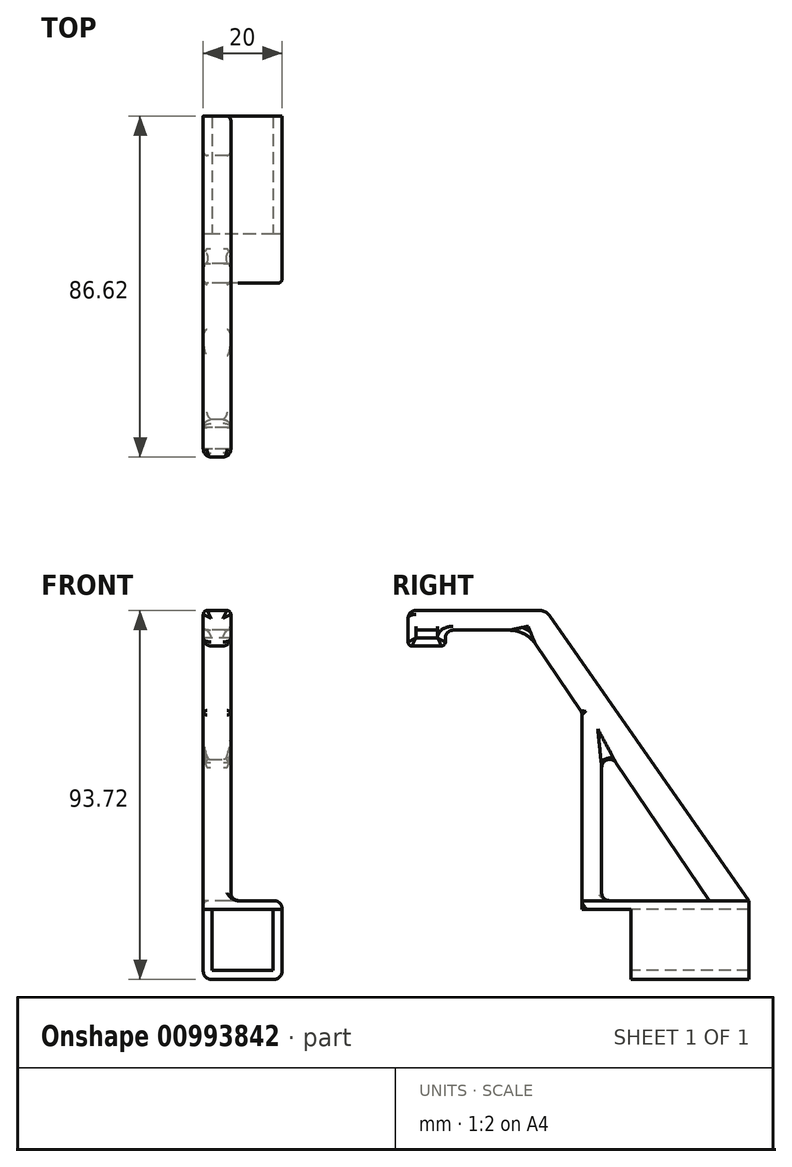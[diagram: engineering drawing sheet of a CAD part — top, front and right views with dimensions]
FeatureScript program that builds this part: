
annotation { "Feature Type Name" : "Feature", "Feature Type Description" : "" }
export const myFeature = defineFeature(function(context is Context, id is Id, definition is map)
    precondition{}
    {
        {
            var Q0;
            Q0=qCreatedBy(makeId("Right.planeOp"),FACE);
            var sketch = newSketch(context, id + "F0", { "sketchPlane" : qUnion([Q0])});
            skLineSegment(sketch, "E0.bottom", {"start": v(-15, 0) * mm, "end": v(15, 0) * mm});
            skLineSegment(sketch, "E0.top", {"start": v(-15, -20) * mm, "end": v(15, -20) * mm});
            skLineSegment(sketch, "E0.left", {"start": v(-15, 0) * mm, "end": v(-15, -20) * mm});
            skLineSegment(sketch, "E0.right", {"start": v(15, 0) * mm, "end": v(15, -20) * mm});
            skLineSegment(sketch, "E1", {"start": v(15, 0) * mm, "end": v(-36.62, 73.72) * mm});
            skLineSegment(sketch, "E2", {"start": v(-36.62, 73.72) * mm, "end": v(-71.62, 73.72) * mm});
            skLineSegment(sketch, "E3", {"start": v(-71.62, 73.72) * mm, "end": v(-71.62, 68.72) * mm});
            skLineSegment(sketch, "E4", {"start": v(-71.62, 68.72) * mm, "end": v(-41.62, 68.72) * mm});
            skLineSegment(sketch, "E5", {"start": v(-41.62, 68.72) * mm, "end": v(5, 0) * mm});
            skLineSegment(sketch, "E6", {"start": v(-15, 0) * mm, "end": v(-27.41, 0) * mm});
            skLineSegment(sketch, "E7", {"start": v(-27.41, 0) * mm, "end": v(-27.41, -2.25) * mm});
            skLineSegment(sketch, "E8", {"start": v(-27.41, -2.25) * mm, "end": v(-15, -2.25) * mm});
            skLineSegment(sketch, "E9", {"start": v(-27.41, 0) * mm, "end": v(-27.41, 47.78) * mm});
            skLineSegment(sketch, "E10", {"start": v(-22.41, 0) * mm, "end": v(-22.41, 40.4) * mm});
            skLineSegment(sketch, "E11", {"start": v(-71.62, 68.72) * mm, "end": v(-71.62, 64.72) * mm});
            skLineSegment(sketch, "E12", {"start": v(-71.62, 64.72) * mm, "end": v(-62.12, 64.72) * mm});
            skLineSegment(sketch, "E13", {"start": v(-62.12, 64.72) * mm, "end": v(-62.12, 68.72) * mm});
            skLineSegment(sketch, "E14", {"start": v(-69.62, 68.72) * mm, "end": v(-69.62, 66.72) * mm});
            skLineSegment(sketch, "E15", {"start": v(-69.62, 66.72) * mm, "end": v(-64.12, 66.72) * mm});
            skLineSegment(sketch, "E16", {"start": v(-64.12, 66.72) * mm, "end": v(-64.12, 68.72) * mm});
            skSolve(sketch);
        }
        {
            var Q0;
            Q0=makeQuery(id+"F0.imprint","IMPRINT",FACE,{"disambiguationData":[TD([[makeQuery(id+"F0.imprint","IMPRINT",EDGE,{"derivedFrom":sQuery(id+"F0.wireOp",EDGE,"E0.top")}),1.0]])]});
            var Q1;
            {var subQ0=sQuery(id+"F0.wireOp",EDGE,"E7");Q1=makeQuery(id+"F0.imprint","IMPRINT",FACE,{"disambiguationData":[TD([[makeQuery(id+"F0.imprint","IMPRINT",EDGE,{"derivedFrom":subQ0}),1.0]])]});}
            extrude(context, id + "F1", {"entities" : qUnion([Q0, Q1]), "depth" : 20 * mm, "offsetDistance" : 25 * mm});
        }
        {
            var Q0;
            {var subQ0=sQuery(id+"F0.wireOp",EDGE,"E1");Q0=makeQuery(id+"F0.imprint","IMPRINT",FACE,{"disambiguationData":[TD([[makeQuery(id+"F0.imprint","IMPRINT",EDGE,{"derivedFrom":subQ0}),1.0]])]});}
            var Q1;
            {var subQ0=sQuery(id+"F0.wireOp",EDGE,"JJyUEpVb-gie7-RlF8-7qWe-H1qUGamomeF3");Q1=makeQuery(id+"F0.imprint","IMPRINT",FACE,{"disambiguationData":[TD([[makeQuery(id+"F0.imprint","IMPRINT",EDGE,{"derivedFrom":subQ0}),-1.0]])]});}
            var Q2;
            {var subQ0=sQuery(id+"F0.wireOp",EDGE,"E9");Q2=makeQuery(id+"F0.imprint","IMPRINT",FACE,{"disambiguationData":[TD([[makeQuery(id+"F0.imprint","IMPRINT",EDGE,{"derivedFrom":subQ0}),-1.0]])]});}
            var Q3;
            {var subQ0=sQuery(id+"F0.wireOp",EDGE,"E11");Q3=makeQuery(id+"F0.imprint","IMPRINT",FACE,{"disambiguationData":[TD([[makeQuery(id+"F0.imprint","IMPRINT",EDGE,{"derivedFrom":subQ0}),1.0]])]});}
            extrude(context, id + "F2", {"entities" : qUnion([Q0, Q1, Q2, Q3]), "operationType" : NewBodyOperationType.ADD, "depth" : 7 * mm, "offsetDistance" : 25 * mm});
        }
        {
            var Q0;
            Q0=makeQuery(id+"F1.opExtrude","SWEPT_FACE",FACE,{"disambiguationData":[OSD([sQuery(id+"F0.wireOp",EDGE,"E0.left")])]});
            var sketch = newSketch(context, id + "F3", { "sketchPlane" : qUnion([Q0])});
            skLineSegment(sketch, "E17.bottom", {"start": v(17.75, -2.25) * mm, "end": v(2.25, -2.25) * mm});
            skLineSegment(sketch, "E17.top", {"start": v(17.75, -17.75) * mm, "end": v(2.25, -17.75) * mm});
            skLineSegment(sketch, "E17.left", {"start": v(17.75, -2.25) * mm, "end": v(17.75, -17.75) * mm});
            skLineSegment(sketch, "E17.right", {"start": v(2.25, -2.25) * mm, "end": v(2.25, -17.75) * mm});
            skPoint(sketch, "E17.middle", {"position": v(0, -10) * mm});
            skSolve(sketch);
        }
        {
            var Q0;
            Q0=makeQuery(id+"F3.imprint","IMPRINT",FACE,{"disambiguationData":[TD([[makeQuery(id+"F3.imprint","IMPRINT",EDGE,{"derivedFrom":sQuery(id+"F3.wireOp",EDGE,"E17.bottom")}),1.0]])]});
            var Q1;
            Q1=makeQuery(id+"F1.opExtrude","SWEPT_FACE",FACE,{"disambiguationData":[OSD([sQuery(id+"F0.wireOp",EDGE,"E0.right")])]});
            extrude(context, id + "F4", {"entities" : qUnion([Q0]), "operationType" : NewBodyOperationType.REMOVE, "endBound" : BoundingType.UP_TO_SURFACE, "oppositeDirection" : true, "depth" : 25 * mm, "endBoundEntityFace" : qUnion([Q1]), "offsetDistance" : 25 * mm});
        }
        {
            var Q0;
            Q0=makeQuery(id+"F2.opExtrude","CAP_EDGE",EDGE,{"disambiguationData":[OSD([sQuery(id+"F0.wireOp",EDGE,"E2")])],"isStart":false});
            var Q1;
            Q1=makeQuery(id+"F2.opExtrude","CAP_EDGE",EDGE,{"disambiguationData":[OSD([sQuery(id+"F0.wireOp",EDGE,"E4")])],"isStart":false});
            var Q2;
            Q2=makeQuery(id+"F2.opExtrude","CAP_EDGE",EDGE,{"disambiguationData":[OSD([sQuery(id+"F0.wireOp",EDGE,"E5")])],"isStart":false});
            var Q3;
            Q3=makeQuery(id+"F2.opExtrude","CAP_EDGE",EDGE,{"disambiguationData":[OSD([sQuery(id+"F0.wireOp",EDGE,"E2")])],"isStart":true});
            var Q4;
            Q4=makeQuery(id+"F2.opExtrude","CAP_EDGE",EDGE,{"disambiguationData":[OSD([sQuery(id+"F0.wireOp",EDGE,"E4")])],"isStart":true});
            var Q5;
            Q5=makeQuery(id+"F2.opExtrude","CAP_EDGE",EDGE,{"disambiguationData":[OSD([sQuery(id+"F0.wireOp",EDGE,"E5")])],"isStart":true});
            var Q6;
            Q6=makeQuery(id+"F2.opExtrude","CAP_EDGE",EDGE,{"disambiguationData":[OSD([sQuery(id+"F0.wireOp",EDGE,"E1")])],"isStart":false});
            var Q7;
            Q7=makeQuery(id+"F2.opExtrude","CAP_EDGE",EDGE,{"disambiguationData":[OSD([sQuery(id+"F0.wireOp",EDGE,"E1")])],"isStart":true});
            var Q8;
            Q8=makeQuery(id+"F2.opExtrude","CAP_EDGE",EDGE,{"disambiguationData":[OSD([sQuery(id+"F0.wireOp",EDGE,"MwvaDB4x-Gc2K-hVEB-6IYb-x19hV3h6sSwj")])],"isStart":false});
            var Q9;
            Q9=makeQuery(id+"F2.opExtrude","CAP_EDGE",EDGE,{"disambiguationData":[OSD([sQuery(id+"F0.wireOp",EDGE,"JJyUEpVb-gie7-RlF8-7qWe-H1qUGamomeF3")])],"isStart":false});
            var Q10;
            Q10=makeQuery(id+"F2.opExtrude","CAP_EDGE",EDGE,{"disambiguationData":[OSD([sQuery(id+"F0.wireOp",EDGE,"MwvaDB4x-Gc2K-hVEB-6IYb-x19hV3h6sSwj")])],"isStart":true});
            var Q11;
            Q11=makeQuery(id+"F2.boolean.opBoolean","MERGE",EDGE,{"derivedFrom":[makeQuery(id+"F1.opExtrude","CAP_EDGE",EDGE,{"disambiguationData":[OSD([sQuery(id+"F0.wireOp",EDGE,"E0.left")])],"isStart":true}),makeQuery(id+"F2.opExtrude","CAP_EDGE",EDGE,{"disambiguationData":[OSD([sQuery(id+"F0.wireOp",EDGE,"JJyUEpVb-gie7-RlF8-7qWe-H1qUGamomeF3")])],"isStart":true})]});
            var Q12;
            Q12=makeQuery(id+"F2.opExtrude","CAP_EDGE",EDGE,{"disambiguationData":[OSD([sQuery(id+"F0.wireOp",EDGE,"E9")])],"isStart":false});
            var Q13;
            Q13=makeQuery(id+"F2.opExtrude","CAP_EDGE",EDGE,{"disambiguationData":[OSD([sQuery(id+"F0.wireOp",EDGE,"E10")])],"isStart":false});
            var Q14;
            Q14=makeQuery(id+"F2.boolean.opBoolean","MERGE",EDGE,{"derivedFrom":[makeQuery(id+"F1.opExtrude","CAP_EDGE",EDGE,{"disambiguationData":[OSD([sQuery(id+"F0.wireOp",EDGE,"E7")])],"isStart":true}),makeQuery(id+"F2.opExtrude","CAP_EDGE",EDGE,{"disambiguationData":[OSD([sQuery(id+"F0.wireOp",EDGE,"E9")])],"isStart":true})]});
            var Q15;
            Q15=makeQuery(id+"F2.opExtrude","CAP_EDGE",EDGE,{"disambiguationData":[OSD([sQuery(id+"F0.wireOp",EDGE,"E10")])],"isStart":true});
            var Q16;
            Q16=makeQuery(id+"F1.opExtrude","CAP_EDGE",EDGE,{"disambiguationData":[OSD([sQuery(id+"F0.wireOp",EDGE,"E7")])],"isStart":false});
            var Q17;
            Q17=makeQuery(id+"F2.opExtrude","SWEPT_EDGE",EDGE,{"disambiguationData":[OSD([sQuery(id+"F0.wireOp",EDGE,"E11"),sQuery(id+"F0.wireOp",EDGE,"E12")])]});
            var Q18;
            Q18=makeQuery(id+"F2.opExtrude","SWEPT_EDGE",EDGE,{"disambiguationData":[OSD([sQuery(id+"F0.wireOp",EDGE,"E12"),sQuery(id+"F0.wireOp",EDGE,"E13")])]});
            fillet(context, id + "F5", {"entities" : qUnion([Q0, Q1, Q2, Q3, Q4, Q5, Q6, Q7, Q8, Q9, Q10, Q11, Q12, Q13, Q14, Q15, Q16, Q17, Q18]), "tangentPropagation" : true, "radius" : 1 * mm, "defaultsChanged" : true, "vertexSettings" : [], "allowEdgeOverflow" : false});
        }
        {
            var Q0;
            Q0=makeQuery(id+"F2.opExtrude","CAP_EDGE",EDGE,{"disambiguationData":[OSD([sQuery(id+"F0.wireOp",EDGE,"E0.bottom")])],"isStart":false});
            var Q1;
            Q1=makeQuery(id+"F5.opFillet","BLEND_EDGE",EDGE,{"blendedFrom":[makeQuery(id+"F2.opExtrude","CAP_EDGE",EDGE,{"disambiguationData":[OSD([sQuery(id+"F0.wireOp",EDGE,"E4")])],"isStart":true}),makeQuery(id+"F2.opExtrude","CAP_EDGE",EDGE,{"disambiguationData":[OSD([sQuery(id+"F0.wireOp",EDGE,"E5")])],"isStart":true})],"blendedInto":[]});
            fillet(context, id + "F6", {"entities" : qUnion([Q0, Q1]), "tangentPropagation" : true, "radius" : 8 * mm, "defaultsChanged" : true, "vertexSettings" : [], "allowEdgeOverflow" : false});
        }
        {
            var Q0;
            Q0=makeQuery(id+"F5.opFillet","BLEND_EDGE",EDGE,{"blendedFrom":[makeQuery(id+"F2.opExtrude","CAP_EDGE",EDGE,{"disambiguationData":[OSD([sQuery(id+"F0.wireOp",EDGE,"E1")])],"isStart":true}),makeQuery(id+"F2.opExtrude","CAP_EDGE",EDGE,{"disambiguationData":[OSD([sQuery(id+"F0.wireOp",EDGE,"E2")])],"isStart":true})],"blendedInto":[]});
            fillet(context, id + "F7", {"entities" : qUnion([Q0]), "tangentPropagation" : true, "radius" : 3 * mm, "defaultsChanged" : false, "vertexSettings" : [], "allowEdgeOverflow" : false});
        }
        {
            var Q0;
            Q0=makeQuery(id+"F1.opExtrude","CAP_EDGE",EDGE,{"disambiguationData":[OSD([sQuery(id+"F0.wireOp",EDGE,"E0.top")])],"isStart":true});
            var Q1;
            Q1=makeQuery(id+"F1.opExtrude","CAP_EDGE",EDGE,{"disambiguationData":[OSD([sQuery(id+"F0.wireOp",EDGE,"E0.top")])],"isStart":false});
            var Q2;
            Q2=makeQuery(id+"F1.opExtrude","CAP_EDGE",EDGE,{"disambiguationData":[OSD([sQuery(id+"F0.wireOp",EDGE,"E0.bottom")])],"isStart":false});
            fillet(context, id + "F8", {"entities" : qUnion([Q0, Q1, Q2]), "radius" : 2 * mm, "defaultsChanged" : false, "vertexSettings" : [], "allowEdgeOverflow" : false});
        }
        {
            var Q0;
            Q0=makeQuery(id+"F5.opFillet","BLEND_EDGE",EDGE,{"blendedFrom":[makeQuery(id+"F2.opExtrude","CAP_EDGE",EDGE,{"disambiguationData":[OSD([sQuery(id+"F0.wireOp",EDGE,"E9")])],"isStart":false}),makeQuery(id+"F1.opExtrude","SWEPT_FACE",FACE,{"disambiguationData":[OSD([sQuery(id+"F0.wireOp",EDGE,"E0.bottom"),sQuery(id+"F0.wireOp",EDGE,"E6")])]})],"blendedInto":[makeQuery(id+"F1.opExtrude","SWEPT_FACE",FACE,{"disambiguationData":[OSD([sQuery(id+"F0.wireOp",EDGE,"E0.bottom"),sQuery(id+"F0.wireOp",EDGE,"E6")])]})]});
            var Q1;
            {var subQ0=sQuery(id+"F0.wireOp",EDGE,"E10");var subQ1=sQuery(id+"F0.wireOp",EDGE,"E5");Q1=makeQuery(id+"F5.opFillet","BLEND_EDGE",EDGE,{"blendedFrom":[makeQuery(id+"F2.opExtrude","CAP_EDGE",EDGE,{"disambiguationData":[OSD([subQ1]),TDD([makeQuery(id+"F0.imprint","IMPRINT",EDGE,{"disambiguationData":[TD([[makeQuery(id+"F0.imprint","INTERSECT",VERTEX,{"derivedFrom":[sQuery(id+"F0.wireOp",EDGE,"E0.bottom"),subQ1]}),1.0]])],"derivedFrom":subQ1})])],"isStart":false}),makeQuery(id+"F2.opExtrude","CAP_EDGE",EDGE,{"disambiguationData":[OSD([subQ0])],"isStart":false})],"blendedInto":[]});}
            var Q2;
            {var subQ0=sQuery(id+"F0.wireOp",EDGE,"E9");var subQ1=sQuery(id+"F0.wireOp",EDGE,"E5");Q2=makeQuery(id+"F5.opFillet","BLEND_EDGE",EDGE,{"blendedFrom":[makeQuery(id+"F2.opExtrude","CAP_EDGE",EDGE,{"disambiguationData":[OSD([subQ1]),TDD([makeQuery(id+"F0.imprint","IMPRINT",EDGE,{"disambiguationData":[TD([[makeQuery(id+"F0.imprint","INTERSECT",VERTEX,{"derivedFrom":[sQuery(id+"F0.wireOp",EDGE,"E4"),subQ1]}),-1.0]])],"derivedFrom":subQ1})])],"isStart":false}),makeQuery(id+"F2.opExtrude","CAP_EDGE",EDGE,{"disambiguationData":[OSD([subQ0])],"isStart":false})],"blendedInto":[]});}
            var Q3;
            Q3=makeQuery(id+"F5.opFillet","BLEND_EDGE",EDGE,{"blendedFrom":[makeQuery(id+"F2.opExtrude","CAP_EDGE",EDGE,{"disambiguationData":[OSD([sQuery(id+"F0.wireOp",EDGE,"E2")])],"isStart":false}),makeQuery(id+"F2.opExtrude","SWEPT_FACE",FACE,{"disambiguationData":[OSD([sQuery(id+"F0.wireOp",EDGE,"E3"),sQuery(id+"F0.wireOp",EDGE,"E11")])]})],"blendedInto":[makeQuery(id+"F2.opExtrude","SWEPT_FACE",FACE,{"disambiguationData":[OSD([sQuery(id+"F0.wireOp",EDGE,"E3"),sQuery(id+"F0.wireOp",EDGE,"E11")])]})]});
            var Q4;
            Q4=makeQuery(id+"F2.opExtrude","SWEPT_EDGE",EDGE,{"disambiguationData":[OSD([sQuery(id+"F0.wireOp",EDGE,"E4"),sQuery(id+"F0.wireOp",EDGE,"E13")])]});
            fillet(context, id + "F9", {"entities" : qUnion([Q0, Q1, Q2, Q3, Q4]), "tangentPropagation" : true, "radius" : 2 * mm, "defaultsChanged" : false, "vertexSettings" : [], "allowEdgeOverflow" : false});
        }
    });
